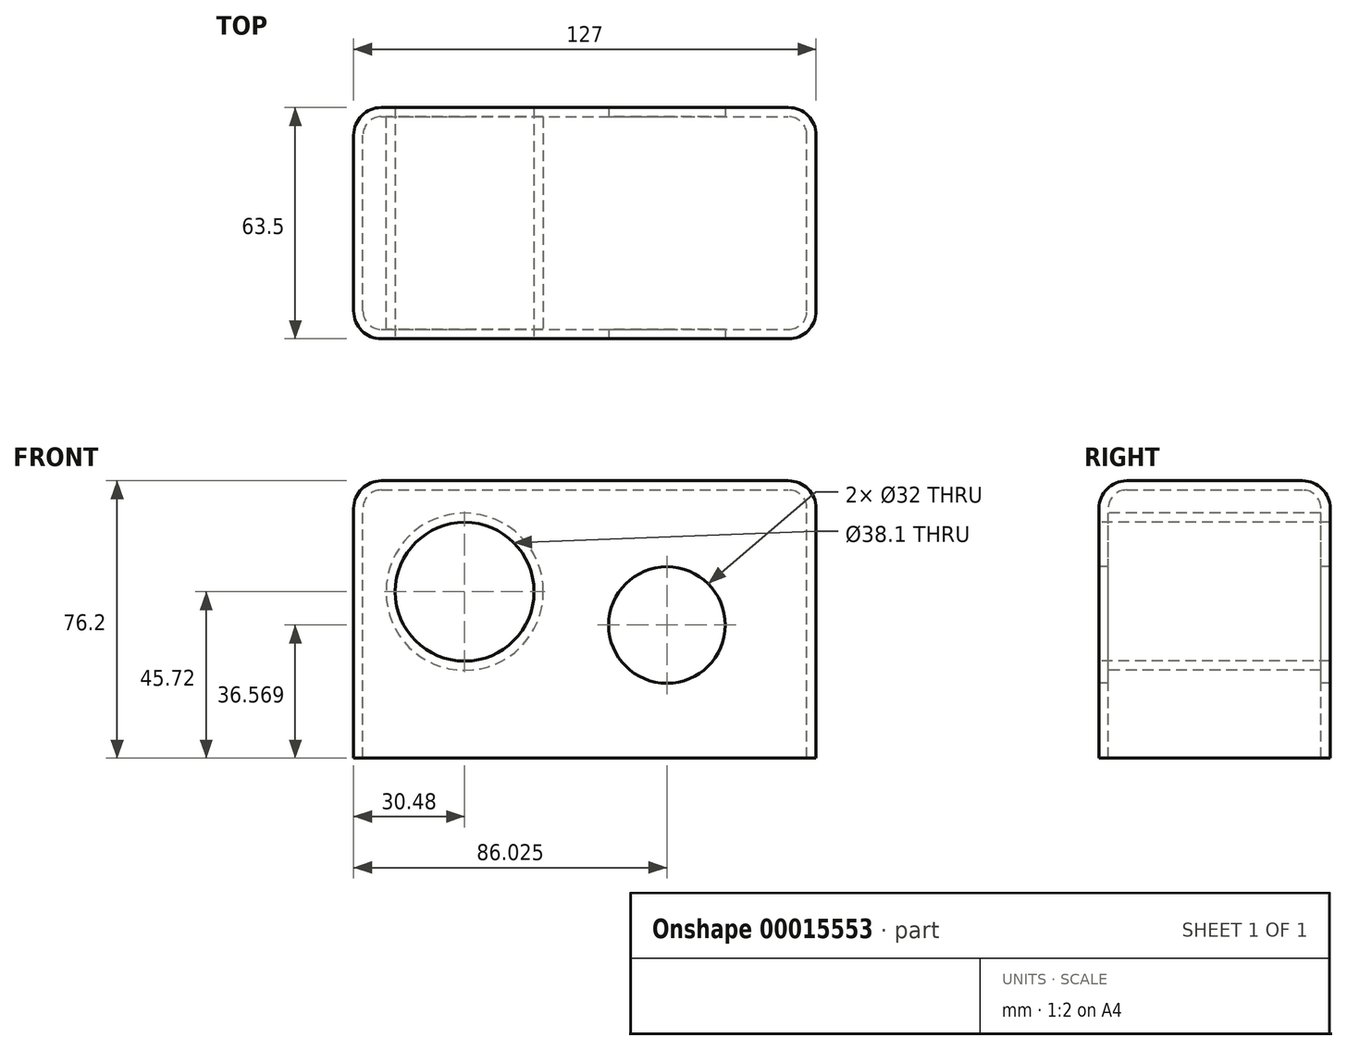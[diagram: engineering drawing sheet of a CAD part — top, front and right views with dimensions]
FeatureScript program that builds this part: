
annotation { "Feature Type Name" : "Feature", "Feature Type Description" : "" }
export const myFeature = defineFeature(function(context is Context, id is Id, definition is map)
    precondition{}
    {
        {
            var Q0;
            Q0=qCreatedBy(makeId("Front.planeOp"),FACE);
            var sketch = newSketch(context, id + "F0", { "sketchPlane" : qUnion([Q0])});
            skLineSegment(sketch, "E0.bottom", {"start": v(0, 0) * mm, "end": v(127, 0) * mm});
            skLineSegment(sketch, "E0.top", {"start": v(0, 76.2) * mm, "end": v(127, 76.2) * mm});
            skLineSegment(sketch, "E0.left", {"start": v(0, 0) * mm, "end": v(0, 76.2) * mm});
            skLineSegment(sketch, "E0.right", {"start": v(127, 0) * mm, "end": v(127, 76.2) * mm});
            skSolve(sketch);
        }
        {
            var Q0;
            Q0=makeQuery(id+"F0.imprint","IMPRINT",FACE,{"disambiguationData":[TD([[makeQuery(id+"F0.imprint","IMPRINT",EDGE,{"derivedFrom":sQuery(id+"F0.wireOp",EDGE,"E0.bottom")}),1.0]])]});
            extrude(context, id + "F1", {"entities" : qUnion([Q0]), "endBound" : BoundingType.SYMMETRIC, "depth" : 63.5 * mm});
        }
        {
            var Q0;
            Q0=makeQuery(id+"F1.opExtrude","CAP_FACE",FACE,{"disambiguationData":[OSD([sQuery(id+"F0.wireOp",EDGE,"E0.bottom"),sQuery(id+"F0.wireOp",EDGE,"E0.top"),sQuery(id+"F0.wireOp",EDGE,"E0.left"),sQuery(id+"F0.wireOp",EDGE,"E0.right")])],"isStart":false});
            var sketch = newSketch(context, id + "F2", { "sketchPlane" : qUnion([Q0])});
            skCircle(sketch, "E1", {"center": v(30.48, 45.72) * mm, "radius": 19.05 * mm});
            skSolve(sketch);
        }
        {
            var Q0;
            Q0=makeQuery(id+"F2.imprint","IMPRINT",FACE,{"disambiguationData":[TD([[makeQuery(id+"F2.imprint","IMPRINT",EDGE,{"derivedFrom":sQuery(id+"F2.wireOp",EDGE,"E1")}),1.0]])]});
            extrude(context, id + "F3", {"entities" : qUnion([Q0]), "operationType" : NewBodyOperationType.REMOVE, "endBound" : BoundingType.THROUGH_ALL, "oppositeDirection" : true, "depth" : 25.4 * mm});
        }
        {
            var Q0;
            Q0=makeQuery(id+"F1.opExtrude","CAP_EDGE",EDGE,{"disambiguationData":[OSD([sQuery(id+"F0.wireOp",EDGE,"E0.top")])],"isStart":false});
            var Q1;
            Q1=makeQuery(id+"F1.opExtrude","CAP_EDGE",EDGE,{"disambiguationData":[OSD([sQuery(id+"F0.wireOp",EDGE,"E0.left")])],"isStart":false});
            var Q2;
            Q2=makeQuery(id+"F1.opExtrude","SWEPT_EDGE",EDGE,{"disambiguationData":[OSD([sQuery(id+"F0.wireOp",EDGE,"E0.top"),sQuery(id+"F0.wireOp",EDGE,"E0.left")])]});
            var Q3;
            Q3=makeQuery(id+"F1.opExtrude","SWEPT_EDGE",EDGE,{"disambiguationData":[OSD([sQuery(id+"F0.wireOp",EDGE,"E0.top"),sQuery(id+"F0.wireOp",EDGE,"E0.right")])]});
            var Q4;
            Q4=makeQuery(id+"F1.opExtrude","CAP_EDGE",EDGE,{"disambiguationData":[OSD([sQuery(id+"F0.wireOp",EDGE,"E0.top")])],"isStart":true});
            var Q5;
            Q5=makeQuery(id+"F1.opExtrude","CAP_EDGE",EDGE,{"disambiguationData":[OSD([sQuery(id+"F0.wireOp",EDGE,"E0.right")])],"isStart":false});
            var Q6;
            Q6=makeQuery(id+"F1.opExtrude","CAP_EDGE",EDGE,{"disambiguationData":[OSD([sQuery(id+"F0.wireOp",EDGE,"E0.right")])],"isStart":true});
            var Q7;
            Q7=makeQuery(id+"F1.opExtrude","CAP_EDGE",EDGE,{"disambiguationData":[OSD([sQuery(id+"F0.wireOp",EDGE,"E0.left")])],"isStart":true});
            fillet(context, id + "F4", {"entities" : qUnion([Q0, Q1, Q2, Q3, Q4, Q5, Q6, Q7]), "radius" : 7.62 * mm, "tangentPropagation" : true, "allowEdgeOverflow" : false});
        }
        {
            var Q0;
            Q0=makeQuery(id+"F1.opExtrude","SWEPT_FACE",FACE,{"disambiguationData":[OSD([sQuery(id+"F0.wireOp",EDGE,"E0.bottom")])]});
            shell(context, id + "F5", {"entities" : qUnion([Q0]), "thickness" : 2.54 * mm});
        }
        {
            var Q0;
            Q0=makeQuery(id+"F1.opExtrude","CAP_FACE",FACE,{"disambiguationData":[OSD([sQuery(id+"F0.wireOp",EDGE,"E0.bottom"),sQuery(id+"F0.wireOp",EDGE,"E0.top"),sQuery(id+"F0.wireOp",EDGE,"E0.left"),sQuery(id+"F0.wireOp",EDGE,"E0.right")])],"isStart":false});
            var sketch = newSketch(context, id + "F6", { "sketchPlane" : qUnion([Q0])});
            skCircle(sketch, "E2", {"center": v(86.03, 36.57) * mm, "radius": 16 * mm});
            skSolve(sketch);
        }
        {
            var Q0;
            Q0=makeQuery(id+"F6.imprint","IMPRINT",FACE,{"disambiguationData":[TD([[makeQuery(id+"F6.imprint","IMPRINT",EDGE,{"derivedFrom":sQuery(id+"F6.wireOp",EDGE,"E2")}),1.0]])]});
            extrude(context, id + "F7", {"entities" : qUnion([Q0]), "operationType" : NewBodyOperationType.REMOVE, "endBound" : BoundingType.THROUGH_ALL, "oppositeDirection" : true, "depth" : 25 * mm});
        }
    });
